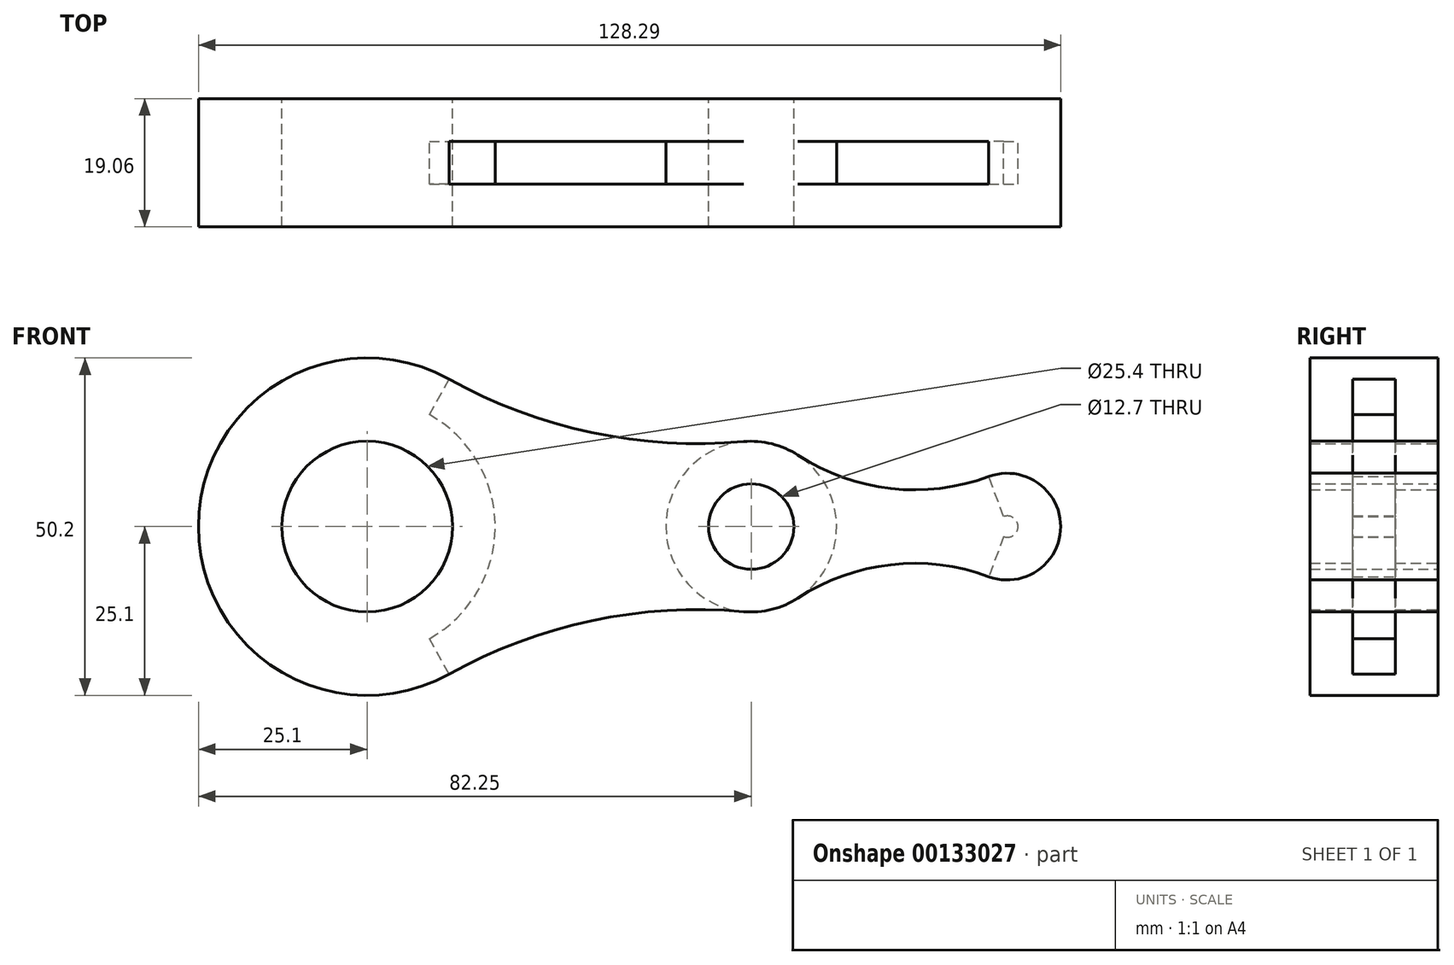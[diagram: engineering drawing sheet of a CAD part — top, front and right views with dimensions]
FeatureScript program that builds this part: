
annotation { "Feature Type Name" : "Feature", "Feature Type Description" : "" }
export const myFeature = defineFeature(function(context is Context, id is Id, definition is map)
    precondition{}
    {
        {
            var Q0;
            Q0=qCreatedBy(makeId("Front.planeOp"),FACE);
            var sketch = newSketch(context, id + "F0", { "sketchPlane" : qUnion([Q0])});
            skArc(sketch, "E0", {"start": v(12.19, 21.94) * mm, "mid": v(-25.1, 0) * mm, "end": v(12.19, -21.94) * mm});
            skArc(sketch, "E1", {"start": v(56.01, -12.65) * mm, "mid": v(60.22, -12.32) * mm, "end": v(64.1, -10.63) * mm});
            skArc(sketch, "E2", {"start": v(92.5, -7.44) * mm, "mid": v(103.19, 0) * mm, "end": v(92.5, 7.44) * mm});
            skArc(sketch, "E3", {"start": v(12.19, 21.94) * mm, "mid": v(33.4, 14) * mm, "end": v(56.01, 12.65) * mm});
            skArc(sketch, "E4", {"start": v(64.1, 10.63) * mm, "mid": v(77.91, 5.66) * mm, "end": v(92.5, 7.44) * mm});
            skArc(sketch, "E5", {"start": v(56.01, -12.65) * mm, "mid": v(33.4, -14) * mm, "end": v(12.19, -21.94) * mm});
            skArc(sketch, "E6", {"start": v(92.5, -7.44) * mm, "mid": v(77.91, -5.66) * mm, "end": v(64.1, -10.63) * mm});
            skArc(sketch, "E7.trimOffspring", {"start": v(64.1, 10.63) * mm, "mid": v(60.22, 12.32) * mm, "end": v(56.01, 12.65) * mm});
            skCircle(sketch, "E8", {"center": v(0, 0) * mm, "radius": 12.7 * mm});
            skCircle(sketch, "E9", {"center": v(57.15, 0) * mm, "radius": 6.35 * mm});
            skSolve(sketch);
        }
        {
            var Q0;
            Q0 = qSketchRegion(id + "F0", true);
            extrude(context, id + "F1", {"entities" : qUnion([Q0]), "endBound" : BoundingType.SYMMETRIC, "depth" : 19.05 * mm});
        }
        {
            var Q0;
            Q0=makeQuery(id+"F1.opExtrude","SWEPT_FACE",FACE,{"disambiguationData":[OSD([sQuery(id+"F0.wireOp",EDGE,"E5")])]});
            var Q1;
            Q1=makeQuery(id+"F1.opExtrude","SWEPT_FACE",FACE,{"disambiguationData":[OSD([sQuery(id+"F0.wireOp",EDGE,"E1")])]});
            var Q2;
            Q2=makeQuery(id+"F1.opExtrude","SWEPT_FACE",FACE,{"disambiguationData":[OSD([sQuery(id+"F0.wireOp",EDGE,"E6")])]});
            var Q3;
            Q3=makeQuery(id+"F1.opExtrude","SWEPT_FACE",FACE,{"disambiguationData":[OSD([sQuery(id+"F0.wireOp",EDGE,"E4")])]});
            var Q4;
            Q4=makeQuery(id+"F1.opExtrude","SWEPT_FACE",FACE,{"disambiguationData":[OSD([sQuery(id+"F0.wireOp",EDGE,"E7.trimOffspring")])]});
            var Q5;
            Q5=makeQuery(id+"F1.opExtrude","SWEPT_FACE",FACE,{"disambiguationData":[OSD([sQuery(id+"F0.wireOp",EDGE,"E3")])]});
            shell(context, id + "F2", {"entities" : qUnion([Q0, Q1, Q2, Q3, Q4, Q5]), "thickness" : 6.35 * mm});
        }
    });
